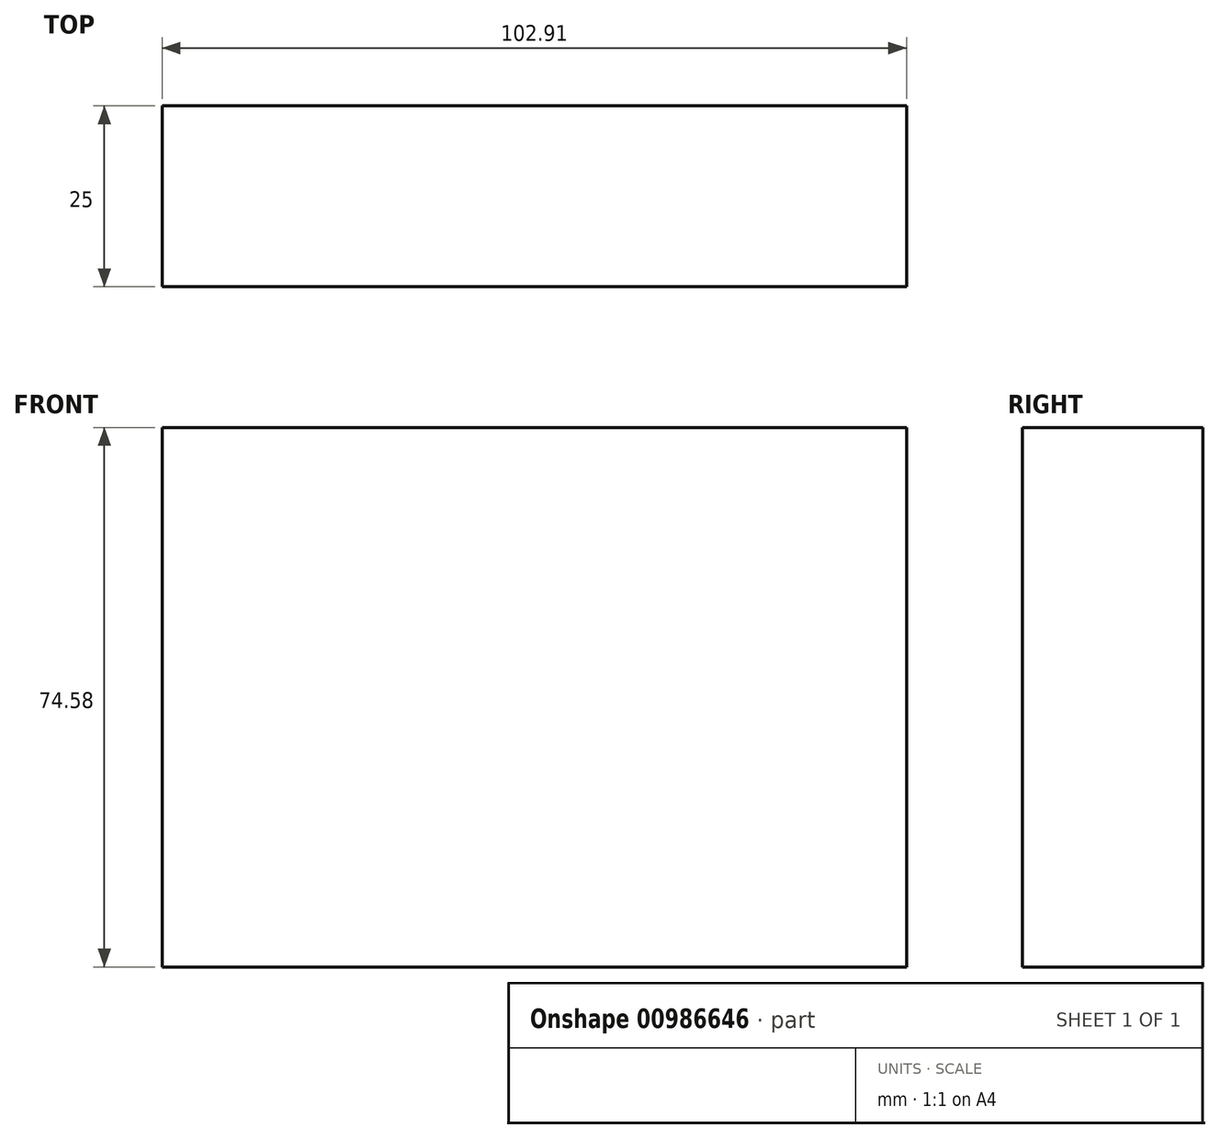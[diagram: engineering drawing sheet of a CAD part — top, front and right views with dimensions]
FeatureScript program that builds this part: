
annotation { "Feature Type Name" : "Feature", "Feature Type Description" : "" }
export const myFeature = defineFeature(function(context is Context, id is Id, definition is map)
    precondition{}
    {
        {
            var Q0;
            Q0=qCreatedBy(makeId("Front.planeOp"),FACE);
            var sketch = newSketch(context, id + "F0", { "sketchPlane" : qUnion([Q0])});
            skLineSegment(sketch, "E0.bottom", {"start": v(-147.57, -7.08) * mm, "end": v(-44.66, -7.08) * mm});
            skLineSegment(sketch, "E0.top", {"start": v(-147.57, 67.5) * mm, "end": v(-44.66, 67.5) * mm});
            skLineSegment(sketch, "E0.left", {"start": v(-147.57, -7.08) * mm, "end": v(-147.57, 67.5) * mm});
            skLineSegment(sketch, "E0.right", {"start": v(-44.66, -7.08) * mm, "end": v(-44.66, 67.5) * mm});
            skPoint(sketch, "E0.middle", {"position": v(-96.12, 30.2) * mm});
            skSolve(sketch);
        }
        {
            var Q0;
            Q0=makeQuery(id+"F0.imprint","IMPRINT",FACE,{"disambiguationData":[TD([[makeQuery(id+"F0.imprint","IMPRINT",EDGE,{"derivedFrom":sQuery(id+"F0.wireOp",EDGE,"E0.bottom")}),1.0]])]});
            extrude(context, id + "F1", {"entities" : qUnion([Q0]), "depth" : 25 * mm, "offsetDistance" : 25 * mm});
        }
    });
